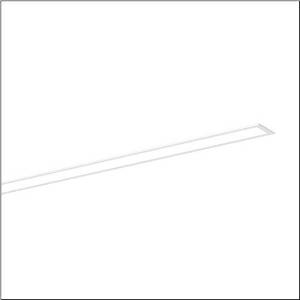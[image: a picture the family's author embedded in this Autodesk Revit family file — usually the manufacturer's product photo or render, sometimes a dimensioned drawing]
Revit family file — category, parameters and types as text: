
# Revit family: silica_r__21_51mx10da42wb_084b
name_source: partatom
category: Lighting Fixtures
units: mm (PartAtom-declared; Revit-internal decimal feet)

## family parameters
Cut with Voids When Loaded = No
Host = Face
Light Source = No
Part Type = Normal
Room Calculation Point = No
Round Connector Dimension = Use Diameter
Shared = No

## types (1)
- --- (1 x LED, 2400 lm, 15.2 W, 4000K)
    Apparent Load = 15 VA
    CIE Flux Codes = 48 79 96 100 100
    Color Rendering = 80
    Color Temperature = 4000K
    Default Elevation = 1800 mm
    Description = Silica® 21, office luminaire, primary optical cover: cover, of PMMA, opal, light emission: direct distribution, primary light characteristic: symmetric, installation type: recessed, LED, rated luminous flux: 2.400lm, luminous efficacy: 158lm/W, light colour: 840, colour temperature: 4000K, control gear: DALI 2, with terminal, 3+2-pole, max. 2.5mm², mains connection: 220..240V, AC, 50/60Hz, rated input power: 15.2W, luminaire housing, of aluminium, traffic white (RAL 9016), length: 1.228mm, width: 79mm, height: 53mm, protection rating (complete): IP20, insulation class (complete): insulation class I (protective earthing), certification: CE, ENEC, VDE, permissible operating ambient temperature: 0..+35°C, standard: EN 50419, packaging unit: 1 piece
    Height = 0 mm  [stored 0 ft]
    Lamp = 1 x LED
    Lamp Light Flux = 2400 lm
    Lamp Power = 15.2 W
    Lamp count = 1
    Length = 1227 mm
    Luminous efficacy = 158 lm/W
    Manufacturer = Siteco
    ModVariant = No
    Model = 51MX10DA42WB
    Mounting Place = Ceiling
    Mounting Type = Recessed
    Number of Poles = 1
    OnlyDefault = Yes
    Power Factor = 1
    Product Name = Silica® 21
    Product group = office luminaire | ceiling recessed
    ProductGroupID = 401
    Protection Class = Protection class I
    Protection Degree = IP 20
    RLX_Detail_Level = 1
    RLX_Emergency_Light_Flux = 0 lm
    RLX_Emergency_Type = 0
    RLX_Emergency_Type_DB = No
    RlxData = <blob elided: 21057 chars, md5=07d6492d>
    Socket = socket
    Standby Power = 0 W
    System Light Flux = 2400 lm
    System Power = 15 W
    Type Comments = factory setting: luminous flux: 100 % | dim-lin: 254 | 218 mA
    Type Image = l_1335891.jpg
    URL = http://relux.com
    VarID = @adj_007463
    Voltage = 0 V
    Weight = 0.00 kg
    Width = 79 mm

note: [stored X ft] marks values corroborated as IEEE doubles in the binary element streams (Revit-internal decimal feet)

## geometry (parser evidence)
native form markers: Blend x4, Sweep x10
no freeform markers — native parametric forms only
